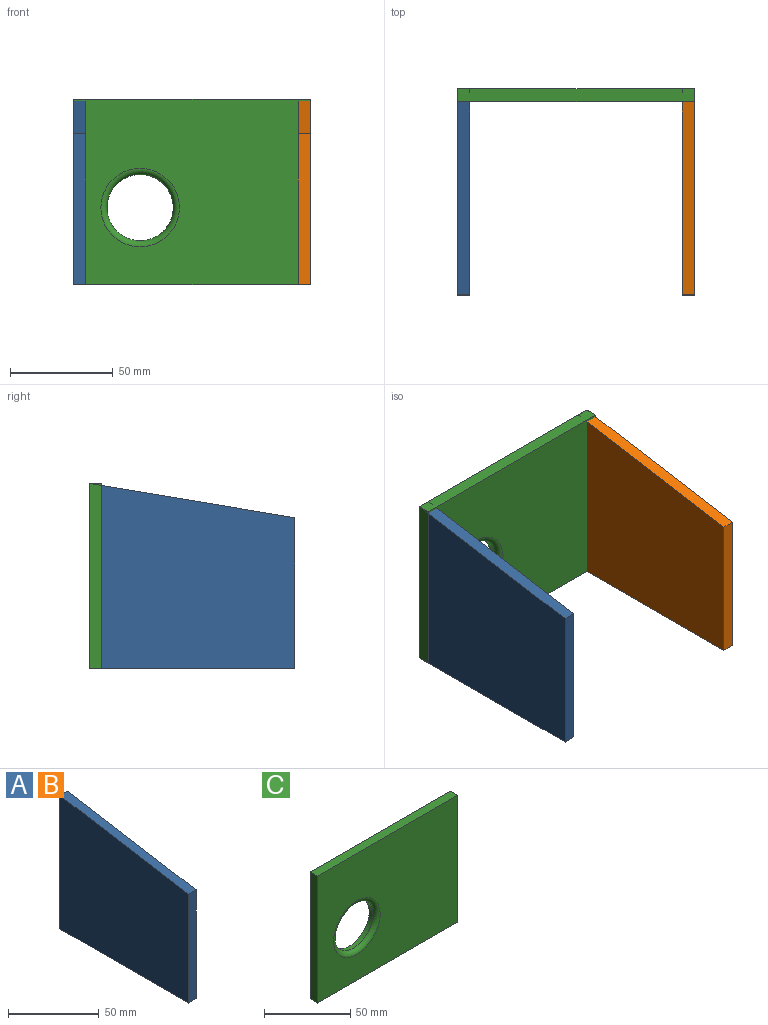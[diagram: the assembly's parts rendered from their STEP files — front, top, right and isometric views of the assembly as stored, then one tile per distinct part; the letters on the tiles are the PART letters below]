
ASSEMBLY  parts=3 mates=1
PART A: 6 faces, bbox 6x100x90 mm
  f0: plane 73.31x6mm, normal (0,-1,0), area 439.8mm2, adj f1,f3,f4,f5
  f1: plane 100x6mm, normal (0,0,-1), area 600mm2, adj f0,f2,f4,f5
  f2: plane 90x6mm, normal (0,1,0), area 540mm2, adj f1,f3,f4,f5
  f3: plane 100x16.69mm, normal (0,-0.16,0.99), area 608.3mm2, adj f0,f2,f4,f5
  f4: plane 100x90mm, normal (1,0,0), area 8165.3mm2, adj f0,f1,f2,f3
  f5: plane 100x90mm, normal (-1,0,0), area 8165.3mm2, adj f0,f1,f2,f3
PART B: same geometry as A
PART C: 8 faces, bbox 115x6x90 mm
  f0: plane 115x6mm, normal (0,0,1), area 690mm2, adj f1,f4,f5,f6
  f1: plane 90x6mm, normal (-1,0,0), area 540mm2, adj f0,f2,f5,f6
  f2: plane 115x6mm, normal (0,0,-1), area 690mm2, adj f1,f4,f5,f6
  f3: cylinder r=16.07mm len=32.13mm, axis (0,1,0), area 302.8mm2, adj f6,f7
  f4: plane 90x6mm, normal (1,0,0), area 540mm2, adj f0,f2,f5,f6
  f5: plane 115x90mm, normal (0,-1,0), area 9208.1mm2, adj f0,f1,f2,f4,f7
  f6: plane 115x90mm, normal (0,1,0), area 9539.2mm2, adj f0,f1,f2,f3,f4
  f7: torus R=19.07mm, axis (0,-1,0), area 508mm2, adj f3,f5
PLACE A t=(-0.81,-68.23,74.14)mm
PLACE B t=(108.19,-68.23,74.14)mm
PLACE C t=(52.57,-0.8,72.09)mm
MATE fastened C.f6 <-> B.f2  axis (0,1,0) through (114.19,-0.8,124.68)mm
